# Revit family: Fixture_Cabinet-Danver-ADA_Sink_Base_Space
name_source: partatom
category: Casework
units: mm (PartAtom-declared; Revit-internal decimal feet)

## family parameters
Always vertical = Yes
Classification Number = 23.40.35.11.11
Cut with Voids When Loaded = No
Room Calculation Point = No
Shared = No
Work Plane-Based = No

## types (1)
- Not a Type - Load Type Catalog
    Base Cabinet = Yes
    Cabinet Material = Metal - Danver - Stainless Steel
    Construction Type = 304 Grade Stainless Steel
    Default Elevation = 0' - 0"
    Depth = 2' - 3"
    Description = Please Load Accompanying Type Catalog (txt.)
    Handle Material = Metal - Danver - Chrome Plated Steel
    Height = 2' - 7 1/4"
    Manufacturer = Danver Outdoor Kitchens
    Model = Please Load Accompanying Type Catalog (txt.)
    Product Documentation Link = https://danver.com
    Product Name = Fixture Cabinet - Danver - ADA Sink Base
    Product Page URL = https://danver.com
    Sink Space = No
    Sink Width = 3' - 9"
    Toe Height = 0' - 0 15/32"
    URL = www.danver.com
    Version = 2019 - V1.0b
    Width = 4' - 0"

## geometry (parser evidence)
native form markers: Sweep x2
no freeform markers — native parametric forms only
